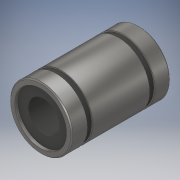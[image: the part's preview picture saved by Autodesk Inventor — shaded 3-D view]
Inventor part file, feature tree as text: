
AUTODESK INVENTOR PART (.ipt)
format: ipt  version: 2019 (Build 230136000, 136)  size: 167,424 bytes
history: native  units: mm
features: extrude x5, sketch x5, other x1, chamfer x1, mirror x1
ambient origin geometry x8: Origin, YZ Plane, XZ Plane, XY Plane, X Axis, Y Axis, Z Axis, Center Point
bodies: Body1 (feature_tree)
feature tree (13):
  other  "Твердое тело1"
  extrude  "Выдавливание1"  Depth=12.0mm
  extrude  "Выдавливание2"  Depth=11.0mm TaperAngle=0.0deg
  extrude  "Выдавливание3"  Depth=11.6mm
  extrude  "Выдавливание4"  Depth=1.0mm TaperAngle=0.0deg
  extrude  "Выдавливание5"  Depth=3.0mm TaperAngle=0.0deg
  chamfer  "Фаска1"  Distance=10.0mm
  mirror  "Зеркальное отражение1"
  sketch  "Эскиз1"
  sketch  "Эскиз2"
  sketch  "Эскиз3"
  sketch  "Эскиз4"
  sketch  "Эскиз5"
